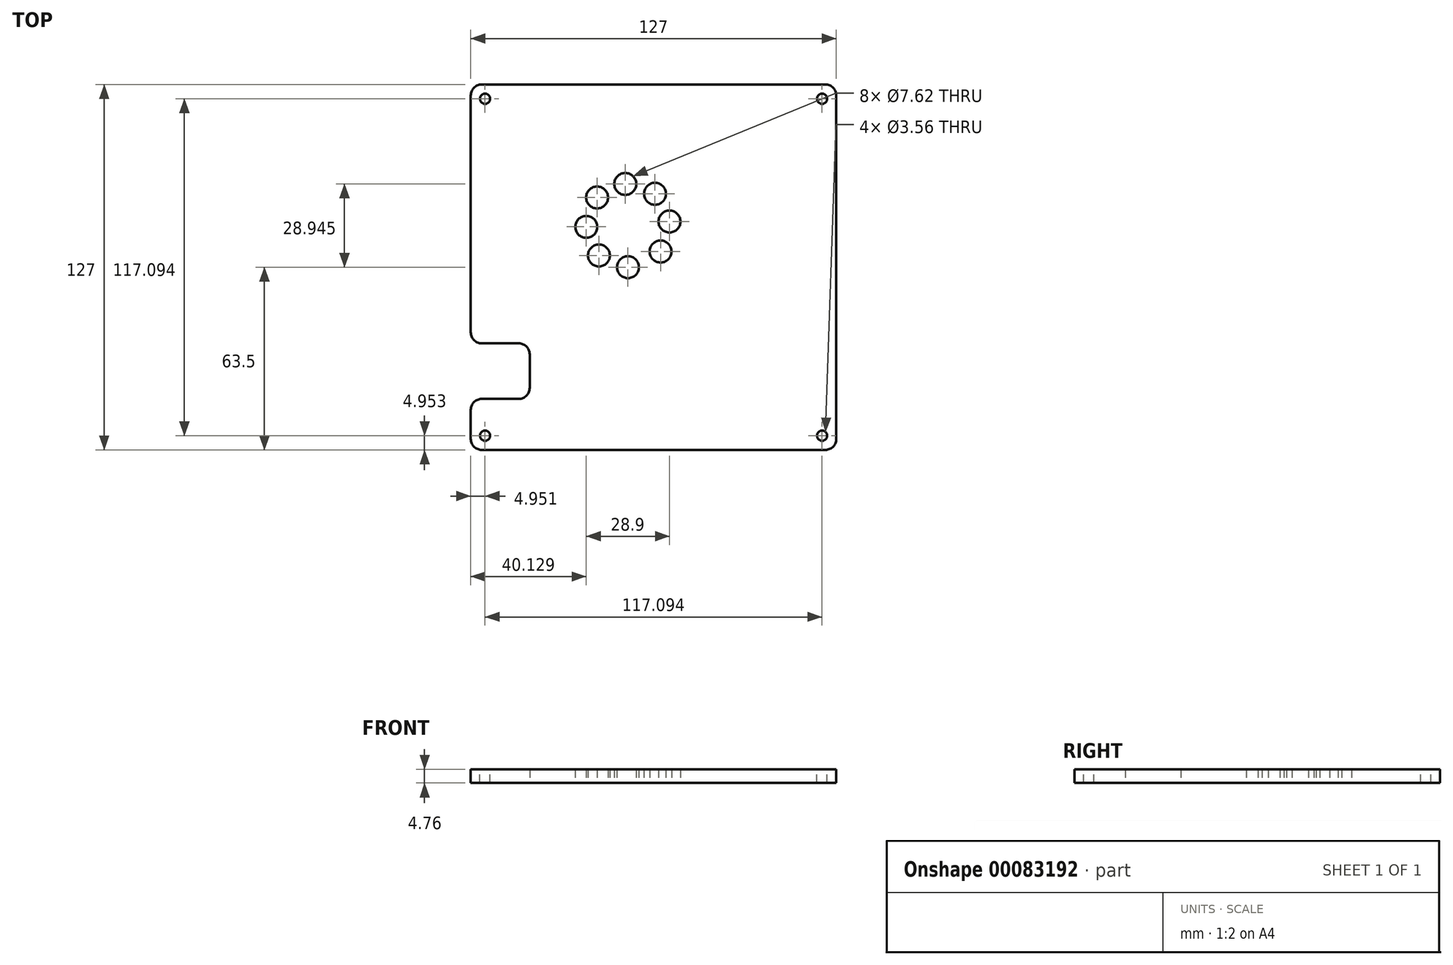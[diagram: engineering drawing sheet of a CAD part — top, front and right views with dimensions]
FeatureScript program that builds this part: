
annotation { "Feature Type Name" : "Feature", "Feature Type Description" : "" }
export const myFeature = defineFeature(function(context is Context, id is Id, definition is map)
    precondition{}
    {
        {
            var Q0;
            Q0=qCreatedBy(makeId("Top.planeOp"),FACE);
            var sketch = newSketch(context, id + "F0", { "sketchPlane" : qUnion([Q0])});
            skLineSegment(sketch, "E0.bottom", {"start": v(-60.26, 63.5) * mm, "end": v(66.74, 63.5) * mm});
            skLineSegment(sketch, "E0.top", {"start": v(-60.26, -63.5) * mm, "end": v(66.74, -63.5) * mm});
            skLineSegment(sketch, "E0.left", {"start": v(-60.26, 63.5) * mm, "end": v(-60.26, -63.5) * mm});
            skLineSegment(sketch, "E0.right", {"start": v(66.74, 63.5) * mm, "end": v(66.74, -63.5) * mm});
            skLineSegment(sketch, "E1.bottom", {"start": v(-60.26, -26.47) * mm, "end": v(-39.79, -26.47) * mm});
            skLineSegment(sketch, "E1.top", {"start": v(-60.26, -45.77) * mm, "end": v(-39.79, -45.77) * mm});
            skLineSegment(sketch, "E1.left", {"start": v(-60.26, -26.47) * mm, "end": v(-60.26, -45.77) * mm});
            skLineSegment(sketch, "E1.right", {"start": v(-39.79, -26.47) * mm, "end": v(-39.79, -45.77) * mm});
            skPoint(sketch, "E2", {"position": v(-5.65, 11.43) * mm});
            skCircle(sketch, "E3", {"center": v(-5.65, 0) * mm, "radius": 3.81 * mm});
            skCircle(sketch, "E4.1.0", {"center": v(-15.73, 4.08) * mm, "radius": 3.81 * mm});
            skCircle(sketch, "E4.2.0", {"center": v(-20.13, 14.02) * mm, "radius": 3.81 * mm});
            skCircle(sketch, "E4.3.0", {"center": v(-16.38, 24.23) * mm, "radius": 3.81 * mm});
            skCircle(sketch, "E4.4.0", {"center": v(-6.58, 28.95) * mm, "radius": 3.81 * mm});
            skCircle(sketch, "E4.5.0", {"center": v(3.74, 25.52) * mm, "radius": 3.8 * mm});
            skCircle(sketch, "E4.6.0", {"center": v(8.77, 15.88) * mm, "radius": 3.81 * mm});
            skPoint(sketch, "E4.center", {"position": v(-5.65, 14.49) * mm});
            skLineSegment(sketch, "E4.anchor1", {"start": v(-5.65, 14.49) * mm, "end": v(-5.65, 0) * mm, "construction": true});
            skLineSegment(sketch, "E4.anchor2", {"start": v(-5.65, 14.49) * mm, "end": v(5.68, 5.45) * mm, "construction": true});
            skCircle(sketch, "E5.1.7.0", {"center": v(5.68, 5.45) * mm, "radius": 3.81 * mm});
            skSolve(sketch);
        }
        {
            var Q0;
            {var subQ4=sQuery(id+"F0.wireOp",EDGE,"E0.bottom");Q0=makeQuery(id+"F0.imprint","IMPRINT",FACE,{"disambiguationData":[TD([[makeQuery(id+"F0.imprint","IMPRINT",EDGE,{"derivedFrom":subQ4}),-1.0]])]});}
            extrude(context, id + "F1", {"entities" : qUnion([Q0]), "depth" : 4.76 * mm});
        }
        {
            var Q0;
            Q0=makeQuery(id+"F1.opExtrude","CAP_FACE",FACE,{"disambiguationData":[OSD([sQuery(id+"F0.wireOp",EDGE,"E0.bottom"),sQuery(id+"F0.wireOp",EDGE,"E0.top"),sQuery(id+"F0.wireOp",EDGE,"E0.left"),sQuery(id+"F0.wireOp",EDGE,"E0.right"),sQuery(id+"F0.wireOp",EDGE,"E1.bottom"),sQuery(id+"F0.wireOp",EDGE,"E1.top"),sQuery(id+"F0.wireOp",EDGE,"E1.right"),sQuery(id+"F0.wireOp",EDGE,"jvWuxKeb-Xfc1-mm2U-hFhp-n1HwOJdSnq8G")])],"isStart":false});
            var sketch = newSketch(context, id + "F2", { "sketchPlane" : qUnion([Q0])});
            skLineSegment(sketch, "E6", {"start": v(-73.48, -58.55) * mm, "end": v(89.15, -58.55) * mm});
            skLineSegment(sketch, "E7", {"start": v(74.55, 58.55) * mm, "end": v(-85.74, 58.55) * mm});
            skLineSegment(sketch, "E8", {"start": v(-55.3, -73.2) * mm, "end": v(-55.3, 77.9) * mm});
            skLineSegment(sketch, "E9", {"start": v(61.79, 75.57) * mm, "end": v(61.79, -76.97) * mm});
            skPoint(sketch, "E10", {"position": v(-55.3, -58.55) * mm});
            skPoint(sketch, "E11", {"position": v(61.79, -58.55) * mm});
            skPoint(sketch, "E12", {"position": v(-55.3, 58.55) * mm});
            skPoint(sketch, "E13", {"position": v(61.79, 58.55) * mm});
            skSolve(sketch);
        }
        {
            var Q0;
            Q0=sQuery(id+"F2.wireOp",VERTEX,"E12");
            var Q1;
            Q1=sQuery(id+"F2.wireOp",VERTEX,"E13");
            var Q2;
            Q2=sQuery(id+"F2.wireOp",VERTEX,"E10");
            var Q3;
            Q3=sQuery(id+"F2.wireOp",VERTEX,"E11");
            var Q4;
            Q4=makeQuery(id+"F1.opExtrude","SWEPT_BODY",BODY,{"disambiguationData":[OSD([sQuery(id+"F0.wireOp",EDGE,"E0.bottom"),sQuery(id+"F0.wireOp",EDGE,"E0.top"),sQuery(id+"F0.wireOp",EDGE,"E0.left"),sQuery(id+"F0.wireOp",EDGE,"E0.right"),sQuery(id+"F0.wireOp",EDGE,"E1.bottom"),sQuery(id+"F0.wireOp",EDGE,"E1.top"),sQuery(id+"F0.wireOp",EDGE,"E1.right"),sQuery(id+"F0.wireOp",EDGE,"jvWuxKeb-Xfc1-mm2U-hFhp-n1HwOJdSnq8G")])]});
            hole(context, id + "F3", {"style" : HoleStyle.SIMPLE, "endStyle" : HoleEndStyle.THROUGH, "holeDiameter" : 3.56 * mm, "locations" : qUnion([Q0, Q1, Q2, Q3]), "scope" : qUnion([Q4]), "isTappedThrough" : true});
        }
        {
            var Q0;
            Q0=makeQuery(id+"F1.opExtrude","SWEPT_EDGE",EDGE,{"disambiguationData":[OSD([sQuery(id+"F0.wireOp",EDGE,"E0.bottom"),sQuery(id+"F0.wireOp",EDGE,"E0.left")])]});
            var Q1;
            Q1=makeQuery(id+"F1.opExtrude","SWEPT_EDGE",EDGE,{"disambiguationData":[OSD([sQuery(id+"F0.wireOp",EDGE,"E0.top"),sQuery(id+"F0.wireOp",EDGE,"E0.left")])]});
            var Q2;
            Q2=makeQuery(id+"F1.opExtrude","SWEPT_EDGE",EDGE,{"disambiguationData":[OSD([sQuery(id+"F0.wireOp",EDGE,"E0.top"),sQuery(id+"F0.wireOp",EDGE,"E0.right")])]});
            var Q3;
            Q3=makeQuery(id+"F1.opExtrude","SWEPT_EDGE",EDGE,{"disambiguationData":[OSD([sQuery(id+"F0.wireOp",EDGE,"E0.bottom"),sQuery(id+"F0.wireOp",EDGE,"E0.right")])]});
            var Q4;
            Q4=makeQuery(id+"F1.opExtrude","SWEPT_EDGE",EDGE,{"disambiguationData":[OSD([sQuery(id+"F0.wireOp",EDGE,"E0.left"),sQuery(id+"F0.wireOp",EDGE,"E1.bottom"),sQuery(id+"F0.wireOp",EDGE,"E1.left")])]});
            var Q5;
            Q5=makeQuery(id+"F1.opExtrude","SWEPT_EDGE",EDGE,{"disambiguationData":[OSD([sQuery(id+"F0.wireOp",EDGE,"E0.left"),sQuery(id+"F0.wireOp",EDGE,"E1.top"),sQuery(id+"F0.wireOp",EDGE,"E1.left")])]});
            var Q6;
            Q6=makeQuery(id+"F1.opExtrude","SWEPT_EDGE",EDGE,{"disambiguationData":[OSD([sQuery(id+"F0.wireOp",EDGE,"E1.bottom"),sQuery(id+"F0.wireOp",EDGE,"E1.right")])]});
            var Q7;
            Q7=makeQuery(id+"F1.opExtrude","SWEPT_EDGE",EDGE,{"disambiguationData":[OSD([sQuery(id+"F0.wireOp",EDGE,"E1.top"),sQuery(id+"F0.wireOp",EDGE,"E1.right")])]});
            fillet(context, id + "F4", {"entities" : qUnion([Q0, Q1, Q2, Q3, Q4, Q5, Q6, Q7]), "radius" : 3.8 * mm, "tangentPropagation" : true, "allowEdgeOverflow" : false});
        }
    });
